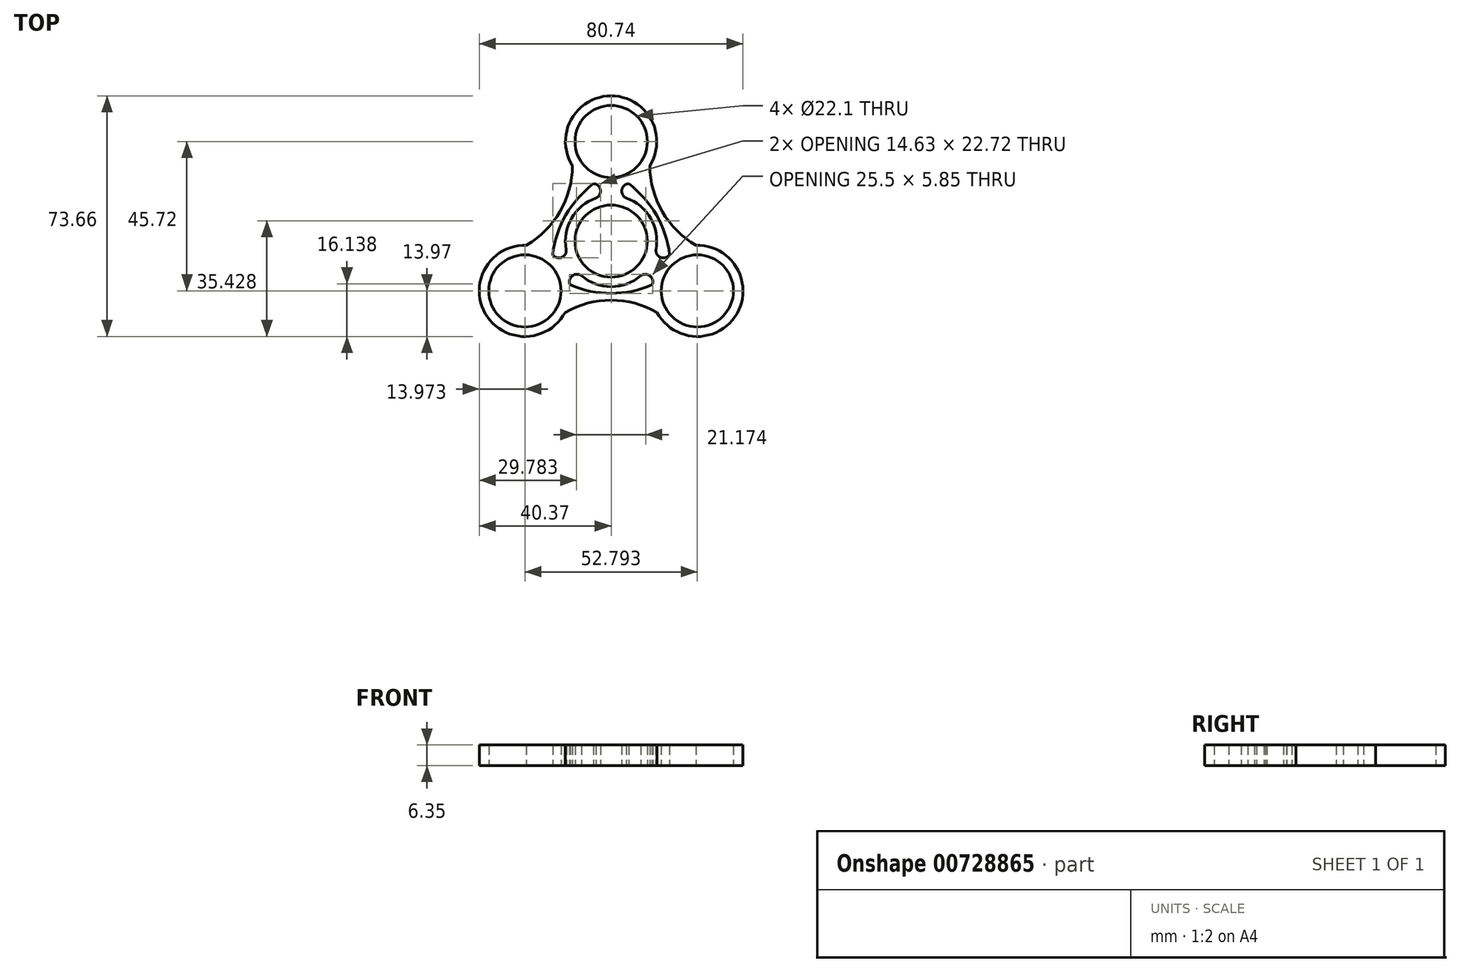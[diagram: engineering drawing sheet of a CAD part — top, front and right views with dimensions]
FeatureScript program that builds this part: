
annotation { "Feature Type Name" : "Feature", "Feature Type Description" : "" }
export const myFeature = defineFeature(function(context is Context, id is Id, definition is map)
    precondition{}
    {
        {
            var Q0;
            Q0=qCreatedBy(makeId("Top.planeOp"),FACE);
            var sketch = newSketch(context, id + "F0", { "sketchPlane" : qUnion([Q0])});
            skCircle(sketch, "E0", {"center": v(0, 0) * mm, "radius": 11.05 * mm});
            skArc(sketch, "E1", {"start": v(-4.61, 13.19) * mm, "mid": v(-12.1, 6.99) * mm, "end": v(-13.73, -2.6) * mm});
            skCircle(sketch, "E2", {"center": v(0, 30.48) * mm, "radius": 11.05 * mm});
            skArc(sketch, "E3", {"start": v(-5.35, 17.58) * mm, "mid": v(-4.79, 17.36) * mm, "end": v(-4.2, 17.16) * mm});
            skCircle(sketch, "E4.1.0", {"center": v(-26.4, -15.24) * mm, "radius": 11.05 * mm});
            skArc(sketch, "E4.1.1", {"start": v(-12.54, -13.43) * mm, "mid": v(-12.64, -12.82) * mm, "end": v(-12.76, -12.22) * mm});
            skCircle(sketch, "E4.2.0", {"center": v(26.4, -15.24) * mm, "radius": 11.05 * mm});
            skArc(sketch, "E4.2.1", {"start": v(17.9, -4.15) * mm, "mid": v(17.42, -4.53) * mm, "end": v(16.96, -4.93) * mm});
            skPoint(sketch, "E5.endSnap0", {"position": v(-14.42, 8.13) * mm});
            skArc(sketch, "E6.1.0", {"start": v(-12.54, -13.43) * mm, "mid": v(0, -16) * mm, "end": v(12.54, -13.43) * mm});
            skArc(sketch, "E6.1.1", {"start": v(14.08, -21.83) * mm, "mid": v(0, -18.07) * mm, "end": v(-14.08, -21.83) * mm});
            skPoint(sketch, "E7.MirrorCS.end.orphan", {"position": v(-7.21, 12.5) * mm});
            skPoint(sketch, "E7.MirrorCS.start.orphan", {"position": v(-5.35, 17.58) * mm});
            skPoint(sketch, "E6.2.2.end.orphan", {"position": v(7.21, 12.5) * mm});
            skPoint(sketch, "E5.end.orphan", {"position": v(-14.42, 0) * mm});
            skPoint(sketch, "E8.orphan", {"position": v(-17.9, -4.15) * mm});
            skPoint(sketch, "E6.2.0.end.orphan", {"position": v(5.35, 17.58) * mm});
            skArc(sketch, "E9.1.0", {"start": v(17.9, -4.15) * mm, "mid": v(13.85, 8) * mm, "end": v(5.35, 17.58) * mm});
            skArc(sketch, "E9.1.1", {"start": v(11.87, 23.1) * mm, "mid": v(15.65, 9.03) * mm, "end": v(25.94, -1.28) * mm});
            skArc(sketch, "E9.2.0", {"start": v(-5.35, 17.58) * mm, "mid": v(-13.85, 8) * mm, "end": v(-17.9, -4.15) * mm});
            skArc(sketch, "E9.2.1", {"start": v(-25.94, -1.28) * mm, "mid": v(-15.65, 9.03) * mm, "end": v(-11.87, 23.1) * mm});
            skArc(sketch, "E10", {"start": v(-4.61, 13.19) * mm, "mid": v(-3.28, 15.67) * mm, "end": v(-5.35, 17.58) * mm});
            skArc(sketch, "E11.MirrorCS", {"start": v(4.61, 13.19) * mm, "mid": v(3.28, 15.67) * mm, "end": v(5.35, 17.58) * mm});
            skArc(sketch, "E12.1.0", {"start": v(-9.11, -10.59) * mm, "mid": v(-11.93, -10.67) * mm, "end": v(-12.54, -13.43) * mm});
            skArc(sketch, "E12.1.1", {"start": v(-13.73, -2.6) * mm, "mid": v(-15.2, -5) * mm, "end": v(-17.9, -4.15) * mm});
            skArc(sketch, "E12.2.0", {"start": v(13.73, -2.6) * mm, "mid": v(15.2, -5) * mm, "end": v(17.9, -4.15) * mm});
            skArc(sketch, "E12.2.1", {"start": v(9.11, -10.59) * mm, "mid": v(11.93, -10.67) * mm, "end": v(12.54, -13.43) * mm});
            skArc(sketch, "E13.trimOffspring", {"start": v(-9.11, -10.59) * mm, "mid": v(0, -13.97) * mm, "end": v(9.11, -10.59) * mm});
            skArc(sketch, "E14.trimOffspring", {"start": v(13.73, -2.6) * mm, "mid": v(12.1, 6.98) * mm, "end": v(4.61, 13.19) * mm});
            skArc(sketch, "E15.trimOffspring", {"start": v(11.87, 23.1) * mm, "mid": v(0, 44.45) * mm, "end": v(-11.87, 23.1) * mm});
            skArc(sketch, "E16.trimOffspring", {"start": v(14.08, -21.83) * mm, "mid": v(38.5, -22.23) * mm, "end": v(25.94, -1.28) * mm});
            skArc(sketch, "E17.trimOffspring", {"start": v(-25.94, -1.28) * mm, "mid": v(-38.5, -22.22) * mm, "end": v(-14.08, -21.83) * mm});
            skArc(sketch, "E18.trimOffspring", {"start": v(-16.96, -4.93) * mm, "mid": v(-17.42, -4.53) * mm, "end": v(-17.9, -4.15) * mm});
            skArc(sketch, "E19.trimOffspring", {"start": v(4.2, 17.16) * mm, "mid": v(4.79, 17.36) * mm, "end": v(5.35, 17.58) * mm});
            skArc(sketch, "E20.trimOffspring", {"start": v(12.76, -12.22) * mm, "mid": v(12.64, -12.82) * mm, "end": v(12.54, -13.43) * mm});
            skSolve(sketch);
        }
        {
            var Q0;
            Q0=qSketchRegion(id+"F0",true);
            extrude(context, id + "F1", {"entities" : qUnion([Q0]), "depth" : 6.35 * mm, "offsetDistance" : 25.4 * mm});
        }
    });
